# Revit family: 4400
name_source: partatom
category: Plumbing Fixtures
units: mm (PartAtom-declared; Revit-internal decimal feet)

## family parameters
Always vertical = Yes
Cut with Voids When Loaded = No
OmniClass Number = 23.45.00.00
OmniClass Title = Sanitary, Laundry, and Cleaning Equipment
Part Type = Normal
Room Calculation Point = No
Round Connector Dimension = Use Diameter
Shared = No
Work Plane-Based = No

## types (3) — shared parameters
Activation = Push Button
Bubbler = Vandal Resistant
CW Connection = No
Description = Outdoor Fountain
Filter = Non Filtered
Fountain = 4400
HW Connection = No
Manufacturer = Elkay
Model = LK4400
Mounting = Floor Mount
Sanitary Flow = 0 GPM
Sanitary Service Size Radius = 0' - 1 1/4"
Type = Outdoor
URL = http://elkayusa.com
Vent Connection = No
Waste Connection = No
Water Service Flow = 0 GPM
Water Service Flow Out = 0 GPM
Water Service Radius = 0' - 0 3/8"
Water Service Size Radius = 0' - 0 3/8"

## type names (no varying parameters)
- 4400
- 4400 FR
- 4400 SAN FR

## geometry (parser evidence)
native form markers: Sweep x5
no freeform markers — native parametric forms only
